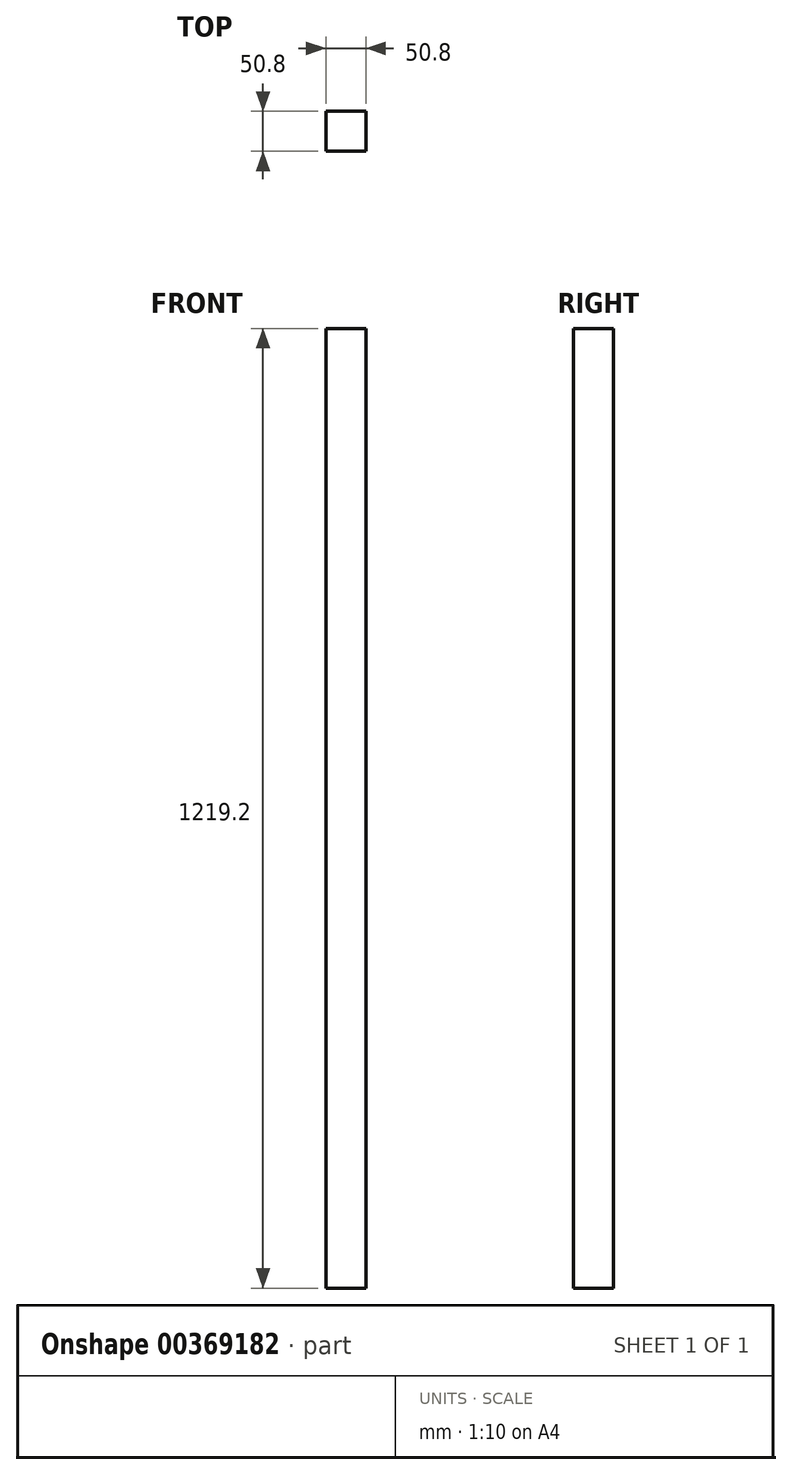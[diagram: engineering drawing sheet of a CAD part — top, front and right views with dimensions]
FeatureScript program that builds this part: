
annotation { "Feature Type Name" : "Feature", "Feature Type Description" : "" }
export const myFeature = defineFeature(function(context is Context, id is Id, definition is map)
    precondition{}
    {
        {
            var Q0;
            Q0=qCreatedBy(makeId("Front.planeOp"),FACE);
            var sketch = newSketch(context, id + "F0", { "sketchPlane" : qUnion([Q0])});
            skLineSegment(sketch, "E0", {"start": v(-602.95, 1149.07) * mm, "end": v(-552.15, 1149.07) * mm});
            skLineSegment(sketch, "E1", {"start": v(-552.15, 1149.07) * mm, "end": v(-552.15, -70.13) * mm});
            skLineSegment(sketch, "E2", {"start": v(-552.15, -70.13) * mm, "end": v(-602.95, -70.13) * mm});
            skLineSegment(sketch, "E3", {"start": v(-602.95, 1149.07) * mm, "end": v(-602.95, -70.13) * mm});
            skSolve(sketch);
        }
        {
            var Q0;
            Q0=makeQuery(id+"F0.imprint","IMPRINT",FACE,{"disambiguationData":[TD([[makeQuery(id+"F0.imprint","IMPRINT",EDGE,{"derivedFrom":sQuery(id+"F0.wireOp",EDGE,"E0")}),-1.0]])]});
            extrude(context, id + "F1", {"entities" : qUnion([Q0]), "depth" : 50.8 * mm});
        }
    });
